# Revit family: QF_ELECTROLUXPROFESSIONAL_1L059Z_TD6-20_E
name_source: partatom
category: Attrezzature speciali
units: mm (PartAtom-declared; Revit-internal decimal feet)

## family parameters
Basato su piano di lavoro = No
Condiviso = No
Punto di calcolo locali = No
Quota connettore circolare = Usa diametro
Sempre verticale = Sì
Taglio con vuoti quando caricato = No
Tipo di parte = Normale

## types (81) — shared parameters
Depth Actual = 1202 mm  [stored 3.94357 ft]
Height Actual = 1771 mm  [stored 5.81037 ft]
Latent Heat Output = 0.0
Length Actual = 790 mm  [stored 2.59186 ft]
Modello = TD6-20
Phase = 3
Produttore = Electrolux Professional
Sensible Heat Output = 0.0
URL = www.electroluxprofessional.com
Weight = 243
zero-valued in all types: Gas KW, Prospetto di default, Steam Pounds per Hour

## per-type parameters (varying)
| type | Cycle | Descrizione | Item Number | Volts | Watts |
| 9873830029 | 50 Hz | TUMBLE DRYER TD6-20 20KG SST DRUM EL 18KW 400/50/3 COMPASS PRO 6G82 EU SILVER DO.RIGHT STOP DISCON. | 1L0EDE | 400 V | 19000 W |
| 9873830019 | 50 Hz | TUMBLE DRYER TD6-20 20KG GALVA.DRUM EL 18KW 400/50/3 COMPASS PRO 6G82 EU SILVER DO.RIGHT STOP DISCON. | 1LSN2M | 400 V | 19000 W |
| 9873830059 | 60 Hz | TUMBLE DRYER TD6-20 20KG GALVA.DRUM EL 13,5KW 208-240/60/3 COMPASS PRO 6G81 EU SILVER DO.RIGHT MB STOP DISCON. | 1L0EH8 | 240 V | 14500 W |
| 9873830229 | 60 Hz | TUMBLE DRYER TD6-20 20KG SST DRUM EL 18KW 400/60/3 COMPASS PRO 6G81 EU SST DO.RIGHT MB STOP DISCON. | 1L0GSW | 400 V | 19000 W |
| 9873830219 | 50 Hz | TUMBLE DRYER TD6-20 20KG GALVA.DRUM EL 18KW 400/50/3N COMPASS PRO 6G81 EU SILVER DO.RIGHT.INS. MB STOP DISCON. EXT.CONN. | 1LSPAK | 400 V | 19000 W |
| 9873830108 | 50 Hz | TUMBLE DRYER TD6-20 MARINE 20KG GALVA.DRUM EL 18KW 400/50/3 COMPASS PRO 6G82 EU SILVER DO.RIGHT STOP DISCON. | 1LSN4U | 400 V | 19000 W |
| 9873830249 | 50 Hz | TUMBLE DRYER TD6-20 20KG GALVA.DRUM EL 18KW 400/50/3N COMPASS PRO 6L80 EU SILVER DO.RIGHT DISCON. | 1LSPLU | 400 V | 19000 W |
| 9873830148 | 60 Hz | TUMBLE DRYER TD6-20 20KG SST DRUM EL 18KW 400/60/3 COMPASS PRO 6G81 EU SILVER DO.RIGHT MB STOP DISCON. | 1LSNFY | 400 V | 19000 W |
| 9873830205 | 50 Hz | TUMBLE DRYER TD6-20 20KG GALVA.DRUM EL 13,5KW 415/50/3N COMPASS PRO 6G82 EU SILVER DO.RIGHT STOP DISCON. | 1LSP92 | 415 V | 14500 W |
| 9873830265 | 60 Hz | TUMBLE DRYER TD6-20 MARINE 20KG GALVA.DRUM EL 13,5KW 208-240/60/3 COMPASS PRO 6G81 SE SST/SILVER DO.RIGHT MB STOP DISCON | 1L82B1 | 240 V | 14500 W |
| 9873830285 | 50 Hz | TUMBLE DRYER TD6-20 20KG GALVA.DRUM EL 18KW 400/50/3N COMPASS PRO 6L80 EU SILVER DO.RIGHT DISCON. | 1L0H88 | 400 V | 19000 W |
| 9873830036 | 60 Hz | TUMBLE DRYER TD6-20 MARINE 20KG SST DRUM EL 18KW 440/60/3 COMPASS PRO 6G82 EU SILVER DO.RIGHT STOP DISCON. | 1L0EDU | 440 V | 19000 W |
| 9873830096 | 50 Hz | TUMBLE DRYER TD6-20 20KG GALVA.DRUM EL 18KW 400/50/3N COMPASS PRO 6L80 EU SILVER DO.RIGHT EXT.PM. DISCON. 2.I/O | 1L80FL | 400 V | 19000 W |
| 9873830286 | 50 Hz | TUMBLE DRYER TD6-20 20KG GALVA.DRUM EL 18KW 400/50/3N COMPASS PRO 6G82 EU SILVER DO.RIGHT.INS. STOP DISCON. EXT.CONN. | 1L0H8H | 400 V | 19000 W |
| 9873830072 | 60 Hz | TUMBLE DRYER TD6-20 MARINE 20KG GALVA.DRUM EL 13,5KW 440/60/3 COMPASS PRO 6G82 SE SST/SILVER DO.LEFT STOP DISCON. EXT.CO | 1L80DN | 440 V | 14500 W |
| 9873830052 | 60 Hz | TUMBLE DRYER TD6-20 20KG GALVA.DRUM EL 13,5KW 400/60/3N COMPASS PRO 6G82 EU SST/SILVER DO.RIGHT STOP DISCON. | 1L0EFN | 400 V | 14500 W |
| 9873830117 | 50 Hz | TUMBLE DRYER TD6-20 20KG GALVA.DRUM EL 18KW 400/50/3N COMPASS PRO 6A81 EU SILVER DO.RIGHT.INS. ELS-NETW. MB DISCON. | 1L8217 | 400 V | 19000 W |
| 9873830272 | 50 Hz | TUMBLE DRYER TD6-20 20KG SST DRUM EL 18KW 200/50/3 COMPASS PRO 6G86 JP SILVER DO.RIGHT DISCON. | 1LT5ZH | 200 V | 19000 W |
| 9873830292 | 60 Hz | TUMBLE DRYER TD6-20 MARINE 20KG SST DRUM EL 18KW 480/60/3 COMPASS PRO 6G81 EU SST DO.LEFT MB STOP DISCON. | 1L0HBP | 480 V | 19000 W |
| 9873830197 | 60 Hz | TUMBLE DRYER TD6-20 MARINE 20KG GALVA.DRUM EL 13,5KW 400/60/3 COMPASS PRO 6G82 EU SST/SILVER DO.LEFT DSC STOP DISCON. EX | 1LSNZJ | 400 V | 14500 W |
| 9873830217 | 50 Hz | TUMBLE DRYER TD6-20 20KG SST DRUM EL 13,5KW 400/50/3N COMPASS PRO 6L80 EU SILVER DO.RIGHT EXT.PM. DISCON. 2.I/O | 1LSPAH | 400 V | 14500 W |
| 9873830057 | 50 Hz | TUMBLE DRYER TD6-20 20KG SST DRUM EL 18KW 400/50/3 COMPASS PRO 6L80 EU SILVER DO.RIGHT EXT.PM. DISCON. 2.I/O | 1L0EGZ | 400 V | 19000 W |
| 9873830047 | 50 Hz | TUMBLE DRYER TD6-20 20KG GALVA.DRUM EL 13,5KW 400/50/3N COMPASS PRO 6A81 SE SILVER DO.LEFT.INS. MB STOP EXT.CONN. | 1L0EED | 400 V | 14500 W |
| 9873830277 | 50 Hz | TUMBLE DRYER TD6-20 20KG SST DRUM EL 18KW 200/50/3 COMPASS PRO 6G86 JP SST/SILVER DO.RIGHT DISCON. | 1L0H80 | 200 V | 19000 W |
| 9873830097 | 50 Hz | TUMBLE DRYER TD6-20 20KG SST DRUM EL 18KW 400/50/3 COMPASS PRO 6G82 EU SST/SILVER DO.LEFT STOP DISCON. | 1L80FX | 400 V | 19000 W |
| 9873830297 | 50 Hz | TUMBLE DRYER TD6-20 20KG SST DRUM EL 18KW 230/50/3 COMPASS PRO 6G81 EU SILVER DO.RIGHT MB STOP DISCON. | 1L0HEL | 230 V | 19000 W |
| 9873830123 | 50 Hz | TUMBLE DRYER TD6-20 MARINE 20KG GALVA.DRUM EL 13,5KW 400/50/3 COMPASS PRO 6G82 SE SST/SILVER DO.LEFT STOP DISCON. | 1L0EL2 | 400 V | 14500 W |
| 9873830113 | 50 Hz | TUMBLE DRYER TD6-20 20KG GALVA.DRUM EL 18KW 400/50/3N COMPASS PRO 6G82 EU SILVER DO.LEFT STOP DISCON. | 1LSN5G | 400 V | 19000 W |
| 9873830173 | 50 Hz | TUMBLE DRYER TD6-20 20KG SST DRUM EL 18KW 400/50/3N COMPASS PRO 6G81 EU SILVER DO.RIGHT.INS. MB DSC AFC STOP DISCON. | 1LSNPU | 400 V | 19000 W |
| 9873830143 | 50 Hz | TUMBLE DRYER TD6-20 20KG SST DRUM EL 18KW 400/50/3N COMPASS PRO 6G81 EU SILVER DO.RIGHT.INS. MB DSC AFC STOP DISCON. | 1LSNDR | 400 V | 19000 W |
| 9873830048 | 50 Hz | TUMBLE DRYER TD6-20 20KG GALVA.DRUM EL 13,5KW 230/50/3 COMPASS PRO 6G81 EU SILVER DO.RIGHT.INS. MB STOP DISCON. EXT.CONN | 1L0EEE | 230 V | 14600 W |
| 9873830098 | 50 Hz | TUMBLE DRYER TD6-20 20KG SST DRUM EL 18KW 230/50/3 COMPASS PRO 6G82 EU SILVER DO.RIGHT STOP DISCON. | 1LSN45 | 230 V | 19000 W |
| 9873830233 | 50 Hz | TUMBLE DRYER TD6-20 20KG SST DRUM EL 18KW 400/50/3 COMPASS PRO 6G81 EU SST DO.RIGHT MB STOP DISCON. | 1LA23M | 400 V | 19000 W |
| 9873830053 | 60 Hz | TUMBLE DRYER TD6-20 MARINE 20KG GALVA.DRUM EL 13,5KW 440/60/3 COMPASS PRO 6G82 SE SILVER DO.LEFT STOP DISCON. | 1L0EFP | 440 V | 14500 W |
| 9873830116 | 50 Hz | TUMBLE DRYER TD6-20 20KG GALVA.DRUM EL 13,5KW 400/50/3N COMPASS PRO 6G82 EU SILVER DO.RIGHT STOP DISCON. | 1LSN69 | 400 V | 14500 W |
| 9873830176 | 50 Hz | TUMBLE DRYER TD6-20 20KG SST DRUM EL 18KW 400/50/3N COMPASS PRO 6L80 EU SILVER DO.LEFT DISCON. | 1LSNSF | 400 V | 19000 W |
| 9873830093 | 50 Hz | TUMBLE DRYER TD6-20 20KG GALVA.DRUM EL 18KW 415/50/3N COMPASS PRO 6G82 EU SILVER DO.LEFT STOP DISCON. | 1L80F1 | 415 V | 19000 W |
| 9873830156 | 60 Hz | TUMBLE DRYER TD6-20 20KG GALVA.DRUM EL 18KW 400/60/3N COMPASS PRO 6G81 EU SILVER DO.RIGHT MB STOP DISCON. | 1L0FW3 | 400 V | 19000 W |
| 9873830218 | 50 Hz | TUMBLE DRYER TD6-20 20KG SST DRUM EL 18KW 400/50/3N COMPASS PRO 6L80 EU SILVER DO.RIGHT EXT.PM. DISCON. 2.I/O | 1LSPAJ | 400 V | 19000 W |
| 9873830208 | 50 Hz | TUMBLE DRYER TD6-20 20KG GALVA.DRUM EL 18KW 400/50/3 COMPASS PRO 6G81 EU SILVER DO.RIGHT MB STOP DISCON. | 1L0GB4 | 400 V | 19000 W |
| 9873830278 | 60 Hz | TUMBLE DRYER TD6-20 20KG SST DRUM EL 18KW 200/60/3 COMPASS PRO 6G86 JP SST/SILVER DO.RIGHT DISCON. | 1L0H81 | 200 V | 19000 W |
| 9873830258 | 50 Hz | TUMBLE DRYER TD6-20 MARINE 20KG SST DRUM EL 18KW 400/50/3 COMPASS PRO 6G82 EU SILVER DO.RIGHT STOP DISCON. | 1L112C | 400 V | 19000 W |
| 9873830248 | 50 Hz | TUMBLE DRYER TD6-20 20KG GALVA.DRUM EL 18KW 415/50/3 COMPASS PRO 6G82 EU SILVER DO.RIGHT STOP DISCON. | 1L0GYE | 415 V | 19000 W |
| 9873830129 | 60 Hz | TUMBLE DRYER TD6-20 20KG GALVA.DRUM EL 18KW 480/60/3 COMPASS PRO 6G81 EU SILVER DO.RIGHT MB STOP DISCON. | 1L0ELV | 480 V | 19000 W |
| 9873830139 | 50 Hz | TUMBLE DRYER TD6-20 20KG SST DRUM EL 13,5KW 400/50/3N COMPASS PRO 6G82 EU SILVER DO.RIGHT STOP DISCON. | 1L0ENN | 400 V | 14500 W |
| 9873830109 | 50 Hz | TUMBLE DRYER TD6-20 20KG SST DRUM EL 18KW 400/50/3N COMPASS PRO 6G81 EU SILVER DO.RIGHT MB AFC STOP DISCON. | 1LSN5E | 400 V | 19000 W |
| 9873830179 | 50 Hz | TUMBLE DRYER TD6-20 20KG SST DRUM EL 18KW 400/50/3 COMPASS PRO 6L80 EU SILVER DO.RIGHT DISCON. | 1LSNSJ | 400 V | 19000 W |
| 9873830189 | 60 Hz | TUMBLE DRYER TD6-20 20KG GALVA.DRUM EL 18KW 400/60/3N COMPASS PRO 6G82 EU SILVER DO.RIGHT STOP DISCON. | 1LSNVB | 400 V | 19000 W |
| 9873830132 | 50 Hz | TUMBLE DRYER TD6-20 20KG SST DRUM EL 13,5KW 400/50/3 COMPASS PRO 6L80 EU SILVER DO.RIGHT EXT.PM. DISCON. 2.I/O | 1L0EMS | 400 V | 14500 W |
| 9873830112 | 50 Hz | TUMBLE DRYER TD6-20 20KG GALVA.DRUM EL 18KW 400/50/3N COMPASS PRO 6G81 EU SILVER DO.RIGHT MB STOP DISCON. | 1LSN59 | 400 V | 19000 W |
| 9873830030 | 50 Hz | TUMBLE DRYER TD6-20 20KG GALVA.DRUM EL 13,5KW 415/50/3N COMPASS PRO 6G81 EU SILVER DO.RIGHT MB STOP DISCON. EXT.CONN. | 1L0EDK | 415 V | 14500 W |
| 9873830010 | 50 Hz | TUMBLE DRYER TD6-20 20KG SST DRUM EL 18KW 400/50/3 COMPASS PRO 6G81 EU SILVER DO.RIGHT.INS. MB STOP DISCON. | 1L0E97 | 400 V | 19000 W |
| 9873830135 | 50 Hz | TUMBLE DRYER TD6-20 20KG SST DRUM EL 18KW 400/50/3N COMPASS PRO 6G82 EU SILVER DO.RIGHT STOP DISCON. | 1LSNAS | 400 V | 19000 W |
| 9873830204 | 50 Hz | TUMBLE DRYER TD6-20 20KG SST DRUM EL 18KW 400/50/3 COMPASS PRO 6G81 EU SILVER DO.RIGHT MB DSC STOP DISCON. | 1LSP81 | 400 V | 19000 W |
| 9873830060 | 60 Hz | TUMBLE DRYER TD6-20 20KG GALVA.DRUM EL 13,5KW 208-240/60/3 COMPASS PRO 6G82 EU SILVER DO.RIGHT STOP DISCON. | 1L0EH9 | 240 V | 14500 W |
| 9873830105 | 60 Hz | TUMBLE DRYER TD6-20 20KG SST DRUM EL 18KW 400/60/3N COMPASS PRO 6L80 EU SILVER DO.RIGHT EXT.PM. DISCON. 2.I/O | 1L80GP | 400 V | 19000 W |
| 9873830254 | 60 Hz | TUMBLE DRYER TD6-20 MARINE 20KG GALVA.DRUM EL 13,5KW 480/60/3 COMPASS PRO 6G82 SE SST/SILVER DO.LEFT STOP DISCON. EXT.CO | 1L0H0H | 480 V | 14500 W |
| 9873830050 | 50 Hz | TUMBLE DRYER TD6-20 20KG GALVA.DRUM EL 13,5KW 400/50/3N COMPASS PRO 6A81 SE SILVER DO.LEFT MB EXT.CONN. | 1L0EG4 | 400 V | 14500 W |
| 9873830155 | 50 Hz | TUMBLE DRYER TD6-20 20KG GALVA.DRUM EL 18KW 230/50/3 COMPASS PRO 6G81 EU SILVER DO.RIGHT MB AFC STOP DISCON. | 1L0FUY | 230 V | 19000 W |
| 9873830040 | 50 Hz | TUMBLE DRYER TD6-20 20KG GALVA.DRUM EL 18KW 400/50/3 COMPASS PRO 6L80 EU SILVER DO.RIGHT DISCON. | 1L0EDX | 400 V | 19000 W |
| 9873830035 | 50 Hz | TUMBLE DRYER TD6-20 20KG SST DRUM EL 13,5KW 415/50/3N COMPASS PRO 6G82 EU SST/SILVER DO.RIGHT STOP DISCON. | 1L0EDT | 415 V | 14500 W |
| 9873830055 | 60 Hz | TUMBLE DRYER TD6-20 MARINE 20KG GALVA.DRUM EL 18KW 480/60/3 COMPASS PRO 6G82 EU SILVER DO.LEFT STOP DISCON. | 1L0EGX | 480 V | 19000 W |
| 9873830220 | 50 Hz | TUMBLE DRYER TD6-20 20KG SST DRUM EL 18KW 400/50/3N COMPASS PRO 6G82 EU SILVER DO.RIGHT STOP DISCON. | 1LSPAL | 400 V | 19000 W |
| 9873830210 | 50 Hz | TUMBLE DRYER TD6-20 20KG SST DRUM EL 18KW 400/50/3N COMPASS PRO 6G81 EU SILVER DO.RIGHT MB STOP DISCON. | 1L0GA4 | 400 V | 19000 W |
| 9873830111 | 50 Hz | TUMBLE DRYER TD6-20 20KG GALVA.DRUM EL 18KW 400/50/3N COMPASS PRO 6G82 EU SILVER DO.RIGHT STOP DISCON. | 1LSN58 | 400 V | 19000 W |
| 9873830151 | 60 Hz | TUMBLE DRYER TD6-20 MARINE 20KG GALVA.DRUM EL 13,5KW 400/60/3 COMPASS PRO 6G82 SE SILVER DO.LEFT STOP DISCON. | 1L0EP8 | 400 V | 14500 W |
| 9873830191 | 60 Hz | TUMBLE DRYER TD6-20 MARINE 20KG GALVA.DRUM EL 13,5KW 230/60/3 COMPASS PRO 6G81 EU SST/SILVER DO.LEFT MB STOP DISCON. EXT | 1LSNVD | 230 V | 14600 W |
| 9873830031 | 50 Hz | TUMBLE DRYER TD6-20 20KG SST DRUM EL 18KW 400/50/3 COMPASS PRO 6G81 EU SILVER DO.RIGHT MB STOP DISCON. | 1L0EDF | 400 V | 19000 W |
| 9873830011 | 60 Hz | TUMBLE DRYER TD6-20 MARINE 20KG GALVA.DRUM EL 13,5KW 440/60/3 COMPASS PRO 6G82 EU SST/SILVER DO.RIGHT.INS. STOP DISCON. | 1L0E98 | 440 V | 14500 W |
| 9873830061 | 60 Hz | TUMBLE DRYER TD6-20 20KG GALVA.DRUM EL 13,5KW 208-240/60/3 COMPASS PRO 6G82 EU SILVER DO.RIGHT STOP DISCON. EXT.CONN. | 1L0EHA | 240 V | 14500 W |
| 9873830051 | 50 Hz | TUMBLE DRYER TD6-20 20KG GALVA.DRUM EL 18KW 400/50/3 COMPASS PRO 6G81 EU SILVER DO.RIGHT MB STOP DISCON. | 1L0EFM | 400 V | 19000 W |
| 9873830041 | 50 Hz | TUMBLE DRYER TD6-20 20KG GALVA.DRUM EL 18KW 400/50/3 COMPASS PRO 6G81 EU SILVER DO.RIGHT.INS. MB STOP DISCON. EXT.CONN. | 1L0EE7 | 400 V | 19000 W |
| 9873830124 | 60 Hz | TUMBLE DRYER TD6-20 20KG SST DRUM EL 18KW 440/60/3 COMPASS PRO 6G82 EU SST DO.RIGHT STOP DISCON. | 1LSN7V | 440 V | 19000 W |
| 9873830144 | 50 Hz | TUMBLE DRYER TD6-20 20KG SST DRUM EL 18KW 400/50/3 COMPASS PRO 6G81 EU SST/SILVER DO.RIGHT.INS. MB STOP DISCON. | 1LSNDS | 400 V | 19000 W |
| 9873830184 | 50 Hz | TUMBLE DRYER TD6-20 20KG GALVA.DRUM EL 13,5KW 400/50/3N COMPASS PRO 6G81 EU SILVER DO.RIGHT MB STOP DISCON. | 1LSNRT | 400 V | 14500 W |
| 9873830221 | 50 Hz | TUMBLE DRYER TD6-20 20KG SST DRUM EL 18KW 400/50/3N COMPASS PRO 6G81 EU SILVER DO.RIGHT.INS. MB STOP DISCON. | 1LSPAM | 400 V | 19000 W |
| 9873830211 | 50 Hz | TUMBLE DRYER TD6-20 20KG GALVA.DRUM EL 18KW 400/50/3N COMPASS PRO 6G81 EU SILVER DO.RIGHT MB STOP DISCON. EXT.CONN. | 1LSPDL | 400 V | 19000 W |
| 9873830130 | 50 Hz | TUMBLE DRYER TD6-20 20KG GALVA.DRUM EL 18KW 400/50/3 COMPASS PRO 6G82 EU SST/SILVER DO.RIGHT STOP DISCON. EXT.CONN. | 1L0ELW | 400 V | 19000 W |
| 9873830201 | 60 Hz | TUMBLE DRYER TD6-20 MARINE 20KG GALVA.DRUM EL 18KW 440/60/3 COMPASS PRO 6G82 EU SILVER DO.RIGHT STOP DISCON. | 1LSP2Y | 440 V | 19000 W |
| 9873830271 | 60 Hz | TUMBLE DRYER TD6-20 20KG SST DRUM EL 18KW 200/60/3 COMPASS PRO 6G86 JP SILVER DO.RIGHT DISCON. | 1LT5ZG | 200 V | 19000 W |
| 9873830140 | 50 Hz | TUMBLE DRYER TD6-20 20KG GALVA.DRUM EL 18KW 230/50/3 COMPASS PRO 6G81 EU SILVER DO.LEFT.INS. MB AFC STOP DISCON. | 1LSNCU | 230 V | 19000 W |

note: [stored X ft] marks values corroborated as IEEE doubles in the binary element streams (Revit-internal decimal feet)

## geometry (parser evidence)
native form markers: Blend x8
no freeform markers — native parametric forms only
